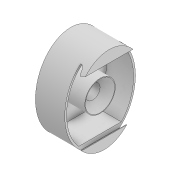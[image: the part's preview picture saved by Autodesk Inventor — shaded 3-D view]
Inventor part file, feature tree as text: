
AUTODESK INVENTOR PART (.ipt)
format: ipt  version: 2022 (Build 260153000, 153)  size: 527,872 bytes
history: native  units: mm
features: reference x7, extrude x6, sketch x6, projected_geometry x2, other x2, chamfer x1
ambient origin geometry x8: Origin, YZ Plane, XZ Plane, XY Plane, X Axis, Y Axis, Z Axis, Center Point
bodies: Volumenkörper1 (feature_tree)
feature tree (24):
  extrude  "Extrusion1"  Depth=0.2mm
  extrude  "Extrusion2"  Depth=0.1mm
  extrude  "Extrusion3"  Depth=0.2mm
  extrude  "Extrusion4"  Depth=24.0mm
  chamfer  "Fase1"  Distance=60.0mm
  extrude  "Extrusion5"  Depth=12.0mm
  extrude  "Extrusion6"  Depth=18.0mm TaperAngle=0.0deg
  sketch  "Skizze1"  dims[d0=0.2mm d1=0.2mm]
  reference  "Referenz1"
  reference  "Referenz2"
  reference  "Referenz3"
  reference  "Referenz4"
  reference  "Referenz5"
  reference  "Referenz6"
  sketch  "Skizze2"  dims[d3=0.1mm d4=0.1mm]
  reference  "Referenz9"
  sketch  "Skizze3"  dims[d5=0.1mm d7=0.2mm]
  sketch  "Skizze4"  dims[d8=6.0mm d9=24.0mm]
  sketch  "Skizze5"  dims[d10=6.0mm d11=60.0mm d12=0.0mm]
  projected_geometry  "Projizierte Kontur1"
  sketch  "Skizze6"  dims[d13=0.0mm d14=0.0mm d15=12.0mm d16=18.0mm d17=0.0mm d18=5.8mm d19=8.0mm d20=0.0mm d21=6.0mm d22=2.0mm d23=45.0deg d24=1.0mm d25=0.0mm d26=0.2mm d27=73.218841mm d28=36.60942mm d30=1.5mm d31=0.5mm d32=22.0mm d33=0.0mm]
  projected_geometry  "Projizierte Kontur2"
  other  "Spectroscope_v0.iam"
  other  "Spectrometer_gratingholder_v0:1"
